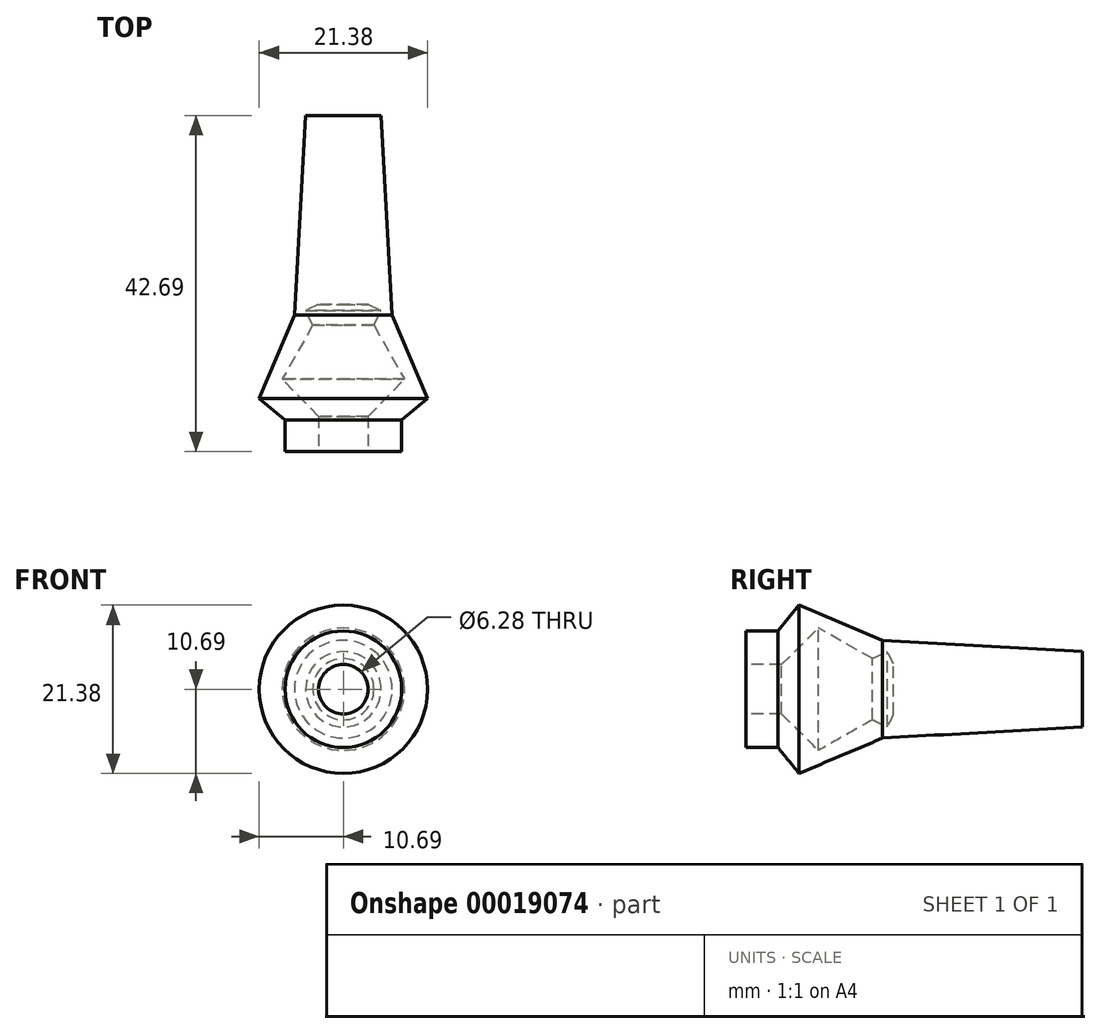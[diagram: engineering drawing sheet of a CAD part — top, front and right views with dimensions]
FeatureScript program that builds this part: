
annotation { "Feature Type Name" : "Feature", "Feature Type Description" : "" }
export const myFeature = defineFeature(function(context is Context, id is Id, definition is map)
    precondition{}
    {
        {
            var Q0;
            Q0=qCreatedBy(makeId("Right.planeOp"),FACE);
            var sketch = newSketch(context, id + "F0", { "sketchPlane" : qUnion([Q0])});
            skLineSegment(sketch, "E0", {"start": v(-11.76, 3.14) * mm, "end": v(-7.27, 3.14) * mm});
            skLineSegment(sketch, "E1", {"start": v(-7.27, 3.14) * mm, "end": v(-2.56, 7.77) * mm});
            skLineSegment(sketch, "E2", {"start": v(-2.56, 7.77) * mm, "end": v(4.31, 3.89) * mm});
            skLineSegment(sketch, "E3", {"start": v(4.31, 3.89) * mm, "end": v(6.18, 4.78) * mm});
            skLineSegment(sketch, "E4", {"start": v(6.18, 4.78) * mm, "end": v(6.95, 3.19) * mm});
            skLineSegment(sketch, "E5", {"start": v(6.95, 3.19) * mm, "end": v(6.95, 0) * mm});
            skLineSegment(sketch, "E6", {"start": v(6.95, 0) * mm, "end": v(30.93, 0) * mm});
            skLineSegment(sketch, "E7", {"start": v(30.93, 0) * mm, "end": v(30.93, 4.78) * mm});
            skLineSegment(sketch, "E8", {"start": v(30.93, 4.78) * mm, "end": v(5.59, 6.2) * mm});
            skLineSegment(sketch, "E9", {"start": v(5.59, 6.2) * mm, "end": v(-5.03, 10.7) * mm});
            skLineSegment(sketch, "E10", {"start": v(-5.03, 10.7) * mm, "end": v(-7.72, 7.4) * mm});
            skLineSegment(sketch, "E11", {"start": v(-7.72, 7.4) * mm, "end": v(-11.76, 7.4) * mm});
            skLineSegment(sketch, "E12", {"start": v(-11.76, 7.4) * mm, "end": v(-11.76, 3.14) * mm});
            skLineSegment(sketch, "E13", {"start": v(-23.42, 0) * mm, "end": v(-17.29, 0) * mm});
            skSolve(sketch);
        }
        {
            var Q0;
            Q0=makeQuery(id+"F0.imprint","IMPRINT",FACE,{"disambiguationData":[TD([[makeQuery(id+"F0.imprint","IMPRINT",EDGE,{"derivedFrom":sQuery(id+"F0.wireOp",EDGE,"E0")}),1.0]])]});
            var Q1;
            Q1=sQuery(id+"F0.wireOp",EDGE,"E13");
            revolve(context, id + "F1", {"entities" : qUnion([Q0]), "axis" : qUnion([Q1]), "revolveType" : RevolveType.FULL});
        }
    });
